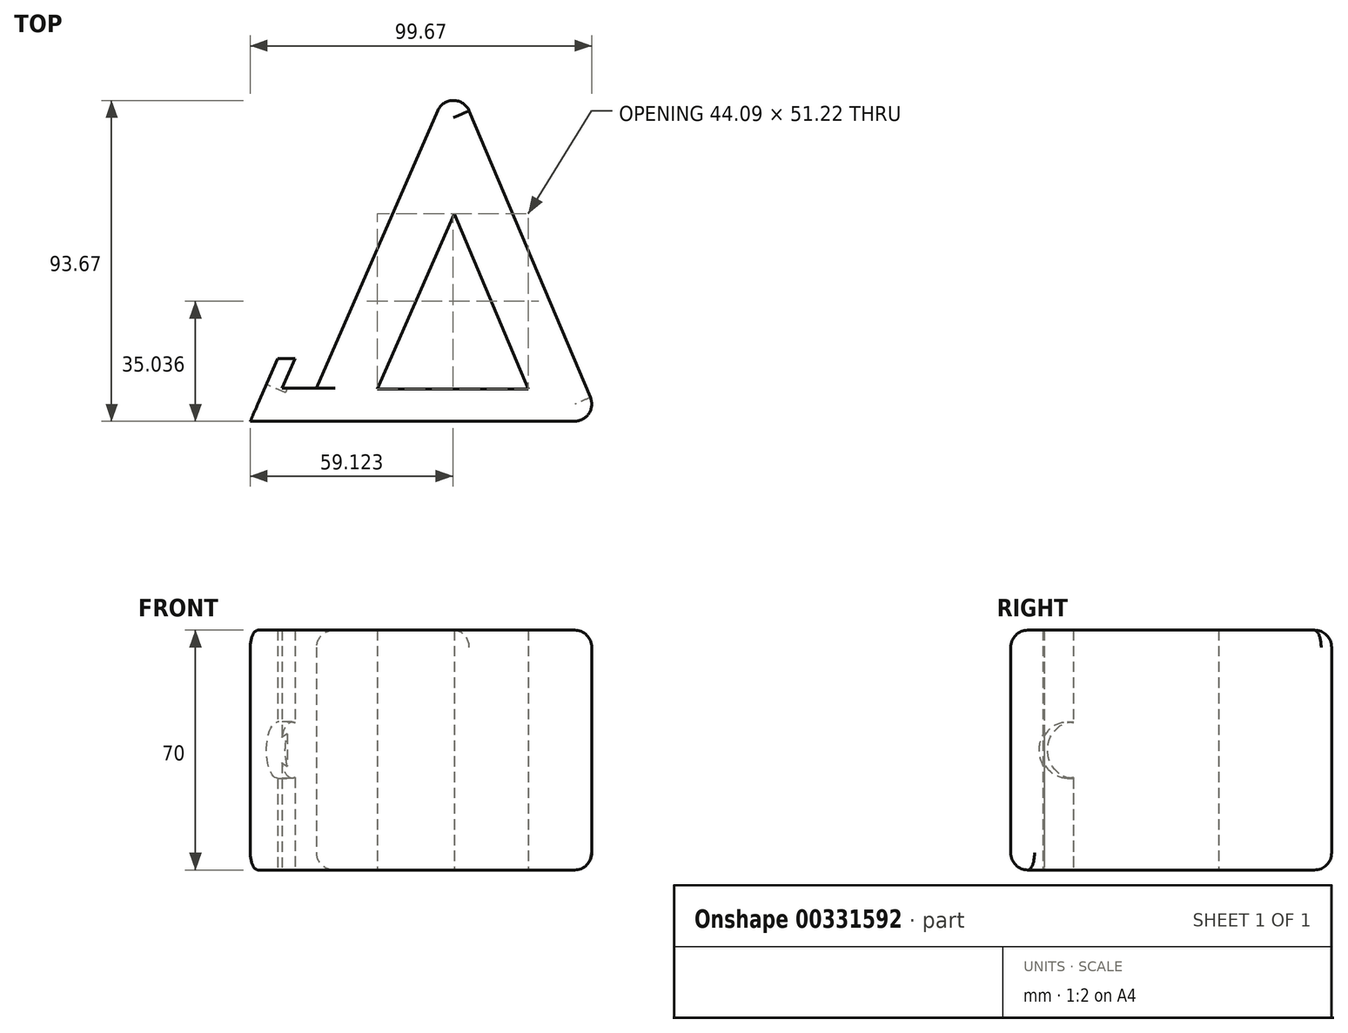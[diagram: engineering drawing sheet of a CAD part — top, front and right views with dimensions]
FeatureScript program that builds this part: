
annotation { "Feature Type Name" : "Feature", "Feature Type Description" : "" }
export const myFeature = defineFeature(function(context is Context, id is Id, definition is map)
    precondition{}
    {
        {
            var Q0;
            Q0=qCreatedBy(makeId("Top.planeOp"),FACE);
            var sketch = newSketch(context, id + "F0", { "sketchPlane" : qUnion([Q0])});
            skLineSegment(sketch, "E0", {"start": v(0, 0) * mm, "end": v(102.21, 0) * mm});
            skLineSegment(sketch, "E1", {"start": v(102.21, 0) * mm, "end": v(59.38, 101.32) * mm});
            skLineSegment(sketch, "E2", {"start": v(59.38, 101.32) * mm, "end": v(19.26, 9.72) * mm});
            skLineSegment(sketch, "E3", {"start": v(19.26, 9.72) * mm, "end": v(9.26, 9.72) * mm});
            skLineSegment(sketch, "E4", {"start": v(9.26, 9.72) * mm, "end": v(13.02, 18.32) * mm});
            skLineSegment(sketch, "E5", {"start": v(13.02, 18.32) * mm, "end": v(8.02, 18.32) * mm});
            skLineSegment(sketch, "E6", {"start": v(8.02, 18.32) * mm, "end": v(0, 0) * mm});
            skSolve(sketch);
        }
        {
            var Q0;
            Q0=makeQuery(id+"F0.imprint","IMPRINT",FACE,{"disambiguationData":[TD([[makeQuery(id+"F0.imprint","IMPRINT",EDGE,{"derivedFrom":sQuery(id+"F0.wireOp",EDGE,"E0")}),1.0]])]});
            extrude(context, id + "F1", {"entities" : qUnion([Q0]), "depth" : 70 * mm});
        }
        {
            var Q0;
            Q0=makeQuery(id+"F1.opExtrude","CAP_EDGE",EDGE,{"disambiguationData":[OSD([sQuery(id+"F0.wireOp",EDGE,"E1")])],"isStart":false});
            var Q1;
            Q1=makeQuery(id+"F1.opExtrude","CAP_EDGE",EDGE,{"disambiguationData":[OSD([sQuery(id+"F0.wireOp",EDGE,"E0")])],"isStart":false});
            fillet(context, id + "F2", {"entities" : qUnion([Q0, Q1]), "radius" : 5 * mm, "tangentPropagation" : true, "allowEdgeOverflow" : false});
        }
        {
            var Q0;
            Q0=makeQuery(id+"F1.opExtrude","CAP_EDGE",EDGE,{"disambiguationData":[OSD([sQuery(id+"F0.wireOp",EDGE,"E2")])],"isStart":false});
            var Q1;
            {var subQ0=sQuery(id+"F0.wireOp",EDGE,"E1");Q1=makeQuery(id+"F2.opFillet","BLEND_EDGE",EDGE,{"blendedFrom":[makeQuery(id+"F1.opExtrude","CAP_EDGE",EDGE,{"disambiguationData":[OSD([subQ0])],"isStart":false}),makeQuery(id+"F1.opExtrude","SWEPT_FACE",FACE,{"disambiguationData":[OSD([subQ0])]})],"blendedInto":[makeQuery(id+"F1.opExtrude","SWEPT_FACE",FACE,{"disambiguationData":[OSD([subQ0])]})]});}
            fillet(context, id + "F3", {"entities" : qUnion([Q0, Q1]), "radius" : 5 * mm, "tangentPropagation" : true, "allowEdgeOverflow" : false});
        }
        {
            var Q0;
            Q0=makeQuery(id+"F1.opExtrude","CAP_EDGE",EDGE,{"disambiguationData":[OSD([sQuery(id+"F0.wireOp",EDGE,"E1")])],"isStart":true});
            var Q1;
            Q1=makeQuery(id+"F1.opExtrude","CAP_EDGE",EDGE,{"disambiguationData":[OSD([sQuery(id+"F0.wireOp",EDGE,"E2")])],"isStart":true});
            fillet(context, id + "F4", {"entities" : qUnion([Q0, Q1]), "radius" : 5 * mm, "tangentPropagation" : true, "allowEdgeOverflow" : false});
        }
        {
            var Q0;
            Q0=makeQuery(id+"F1.opExtrude","CAP_EDGE",EDGE,{"disambiguationData":[OSD([sQuery(id+"F0.wireOp",EDGE,"E0")])],"isStart":true});
            fillet(context, id + "F5", {"entities" : qUnion([Q0]), "radius" : 5 * mm, "tangentPropagation" : true, "allowEdgeOverflow" : false});
        }
        {
            var Q0;
            Q0=makeQuery(id+"F1.opExtrude","SWEPT_FACE",FACE,{"disambiguationData":[OSD([sQuery(id+"F0.wireOp",EDGE,"E6")])]});
            var sketch = newSketch(context, id + "F6", { "sketchPlane" : qUnion([Q0])});
            skCircle(sketch, "E7", {"center": v(-20, 35) * mm, "radius": 8.26 * mm});
            skSolve(sketch);
        }
        {
            var Q0;
            {var subQ0=sQuery(id+"F6.wireOp",EDGE,"E7");var subQ1=makeQuery(id+"F1.opExtrude","SWEPT_EDGE",EDGE,{"disambiguationData":[OSD([sQuery(id+"F0.wireOp",EDGE,"E5"),sQuery(id+"F0.wireOp",EDGE,"E6")])]});var subQ2=makeQuery(id+"F6.imprint","INTERSECT",VERTEX,{"disambiguationData":[OD(0.0)],"derivedFrom":[subQ1,subQ0]});Q0=makeQuery(id+"F6.imprint","IMPRINT",FACE,{"disambiguationData":[TD([[makeQuery(id+"F6.imprint","IMPRINT",EDGE,{"disambiguationData":[TD([[subQ2,1.0]])],"derivedFrom":subQ0}),1.0]])]});}
            var Q1;
            {var subQ0=sQuery(id+"F6.wireOp",EDGE,"E7");var subQ1=makeQuery(id+"F1.opExtrude","SWEPT_EDGE",EDGE,{"disambiguationData":[OSD([sQuery(id+"F0.wireOp",EDGE,"E5"),sQuery(id+"F0.wireOp",EDGE,"E6")])]});var subQ2=makeQuery(id+"F6.imprint","INTERSECT",VERTEX,{"disambiguationData":[OD(0.0)],"derivedFrom":[subQ1,subQ0]});Q1=makeQuery(id+"F6.imprint","IMPRINT",FACE,{"disambiguationData":[TD([[makeQuery(id+"F6.imprint","IMPRINT",EDGE,{"disambiguationData":[TD([[subQ2,-1.0]])],"derivedFrom":subQ0}),1.0]])]});}
            extrude(context, id + "F7", {"entities" : qUnion([Q0, Q1]), "operationType" : NewBodyOperationType.REMOVE, "oppositeDirection" : true, "depth" : 6 * mm});
        }
        {
            var Q0;
            Q0=makeQuery(id+"F1.opExtrude","CAP_FACE",FACE,{"disambiguationData":[OSD([sQuery(id+"F0.wireOp",EDGE,"E0"),sQuery(id+"F0.wireOp",EDGE,"E1"),sQuery(id+"F0.wireOp",EDGE,"E2"),sQuery(id+"F0.wireOp",EDGE,"E3"),sQuery(id+"F0.wireOp",EDGE,"E4"),sQuery(id+"F0.wireOp",EDGE,"E5"),sQuery(id+"F0.wireOp",EDGE,"E6")])],"isStart":true});
            var sketch = newSketch(context, id + "F8", { "sketchPlane" : qUnion([Q0])});
            skLineSegment(sketch, "E8", {"start": v(37.08, -9.42) * mm, "end": v(81.17, -9.42) * mm});
            skLineSegment(sketch, "E9", {"start": v(81.17, -9.42) * mm, "end": v(59.52, -60.65) * mm});
            skLineSegment(sketch, "E10", {"start": v(59.52, -60.65) * mm, "end": v(37.08, -9.42) * mm});
            skSolve(sketch);
        }
        {
            var Q0;
            Q0 = qSketchRegion(id + "F8", true);
            var Q1;
            Q1=makeQuery(id+"F8.imprint","IMPRINT",FACE,{"disambiguationData":[TD([[makeQuery(id+"F8.imprint","IMPRINT",EDGE,{"derivedFrom":sQuery(id+"F8.wireOp",EDGE,"E8")}),-1.0]])]});
            extrude(context, id + "F9", {"entities" : qUnion([Q0, Q1]), "operationType" : NewBodyOperationType.REMOVE, "endBound" : BoundingType.THROUGH_ALL, "oppositeDirection" : true, "depth" : 25 * mm});
        }
    });
